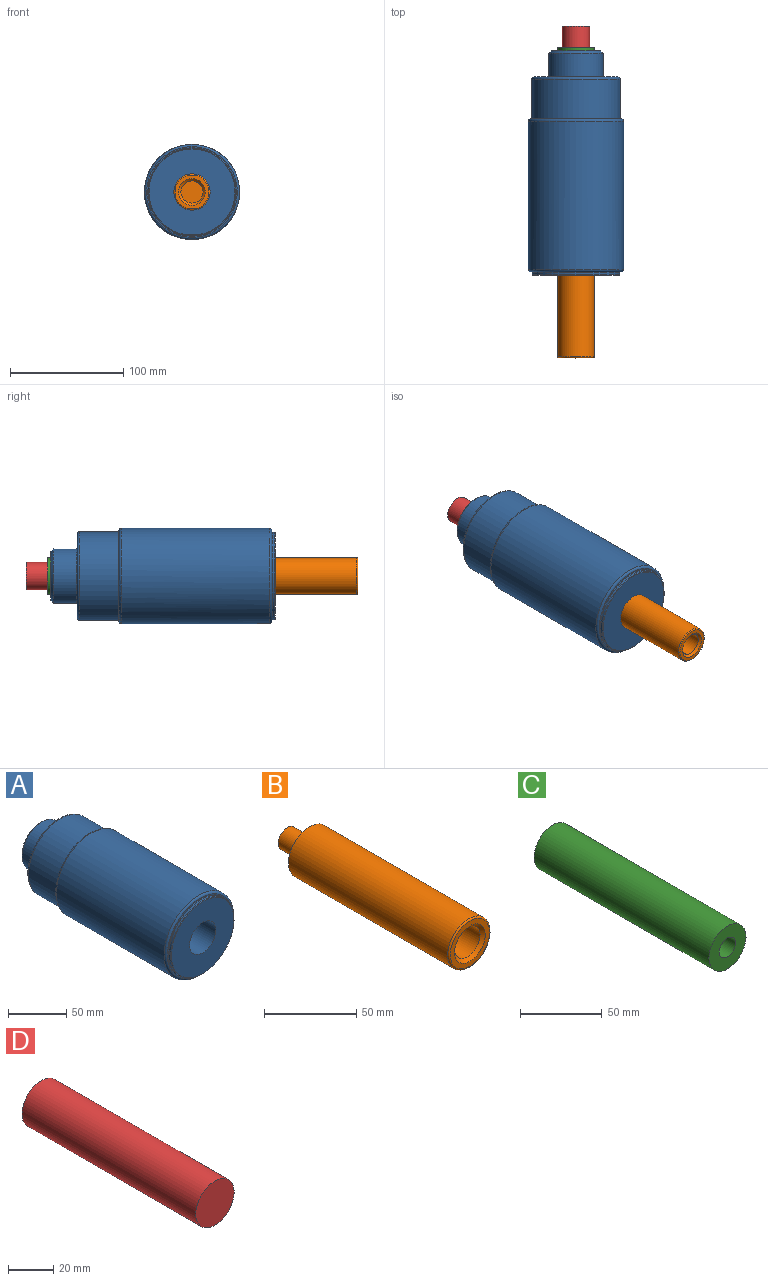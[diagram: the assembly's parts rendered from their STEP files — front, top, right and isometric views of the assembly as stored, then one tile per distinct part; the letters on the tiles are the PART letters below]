
ASSEMBLY  parts=4 mates=3
PART A: 20 faces, bbox 90.9x198x90.9 mm
  f0: plane 44x44mm, normal (0,1,0), area 530.7mm2, adj f9,f19
  f1: cylinder r=24mm len=48mm, axis (0,1,0), area 3091.3mm2, adj f15,f19
  f2: plane 74x74mm, normal (0,1,0), area 2415.1mm2, adj f12,f15
  f3: cylinder r=39mm len=78mm, axis (0,1,0), area 8454mm2, adj f12,f16
  f4: plane 80x80mm, normal (0,1,0), area 124.9mm2, adj f13,f16
  f5: cylinder r=42mm len=131mm, axis (0,1,0), area 34570.1mm2, adj f13,f14
  f6: plane 80x80mm, normal (0,-1,0), area 248.2mm2, adj f14,f17
  f7: cylinder r=38.5mm len=77mm, axis (0,1,0), area 483.8mm2, adj f17,f18
  f8: plane 76x76mm, normal (0,-1,0), area 3732.2mm2, adj f11,f18
  f9: cylinder r=17.75mm len=148mm, axis (0,1,0), area 16505.9mm2, adj f0,f10
  f10: plane 35.5x35.5mm, normal (0,1,0), area 185.6mm2, adj f9,f11
  f11: cylinder r=16mm len=50mm, axis (0,-1,0), area 5026.5mm2, adj f8,f10
  f12: torus R=37mm, axis (0,-1,0), area 755.5mm2, adj f2,f3
  f13: torus R=40mm, axis (0,-1,0), area 814.7mm2, adj f4,f5
  f14: torus R=40mm, axis (0,1,0), area 814.7mm2, adj f5,f6
  f15: torus R=24.5mm, axis (0,-1,0), area 119.3mm2, adj f1,f2
  f16: torus R=39.5mm, axis (0,-1,0), area 193.4mm2, adj f3,f4
  f17: torus R=39mm, axis (0,1,0), area 190.9mm2, adj f6,f7
  f18: torus R=38mm, axis (0,1,0), area 189.1mm2, adj f7,f8
  f19: cone r=22mm half-angle=45deg, axis (0,-1,0), area 408.7mm2, adj f0,f1
PART B: 9 faces, bbox 34.6x140x34.6 mm
  f0: cylinder r=16mm len=122mm, axis (0,1,0), area 12264.8mm2, adj f2,f5
  f1: plane 30x30mm, normal (0,-1,0), area 273.1mm2, adj f5,f8
  f2: plane 32x32mm, normal (0,1,0), area 650.3mm2, adj f0,f3
  f3: cylinder r=7mm len=17mm, axis (0,-1,0), area 747.7mm2, adj f2,f4
  f4: plane 14x14mm, normal (0,1,0), area 153.9mm2, adj f3
  f5: torus R=15mm, axis (0,1,0), area 154.3mm2, adj f0,f1
  f6: cylinder r=9.75mm len=83mm, axis (0,-1,0), area 5084.7mm2, adj f7,f8
  f7: plane 19.5x19.5mm, normal (0,-1,0), area 298.6mm2, adj f6
  f8: cone r=9.75mm half-angle=45deg, axis (0,-1,0), area 191mm2, adj f1,f6
PART C: 11 faces, bbox 32x151x32 mm
  f0: plane 25x25mm, normal (0,-1,0), area 144.5mm2, adj f5,f7
  f1: cylinder r=7mm len=71mm, axis (0,-1,0), area 3122.7mm2, adj f4,f6
  f2: cylinder r=16mm len=151mm, axis (0,-1,0), area 15180.2mm2, adj f3,f4
  f3: plane 32x32mm, normal (0,1,0), area 273.3mm2, adj f2,f8
  f4: plane 32x32mm, normal (0,-1,0), area 650.3mm2, adj f1,f2
  f5: cylinder r=12.5mm len=50mm, axis (0,1,0), area 3927mm2, adj f0,f6
  f6: plane 25x25mm, normal (0,1,0), area 336.9mm2, adj f1,f5
  f7: cylinder r=10.5mm len=23mm, axis (0,1,0), area 1517.4mm2, adj f0,f10
  f8: cylinder r=13mm len=26mm, axis (0,1,0), area 408.4mm2, adj f3,f9
  f9: plane 26x26mm, normal (0,1,0), area 40.1mm2, adj f8,f10
  f10: cone r=10.5mm half-angle=45deg, axis (0,1,0), area 204.4mm2, adj f7,f9
PART D: 3 faces, bbox 24x109x24 mm
  f0: cylinder r=12mm len=109mm, axis (0,-1,0), area 8218.4mm2, adj f1,f2
  f1: plane 24x24mm, normal (0,1,0), area 452.4mm2, adj f0
  f2: plane 24x24mm, normal (0,-1,0), area 452.4mm2, adj f0
PLACE A t=(-123.61,-88.55,60.77)mm fixed
PLACE B rot(axis=(0,1,0),33.6deg) t=(-123.61,-88.55,60.77)mm
PLACE C rot(axis=(0,1,0),123.6deg) t=(-123.61,-88.55,60.77)mm
PLACE D rot(axis=(0,-1,0),168.7deg) t=(-123.61,-148.55,60.77)mm
MATE fastened B.f0 <-> C.f1  axis (0,1,0) through (-123.61,-38.55,60.77)mm
MATE cylindrical C.f1 <-> D.f0  axis (0,1,0) through (-123.61,82.45,60.77)mm
MATE cylindrical A.f1 <-> B.f0  axis (0,1,0) through (-123.61,-38.55,60.77)mm
